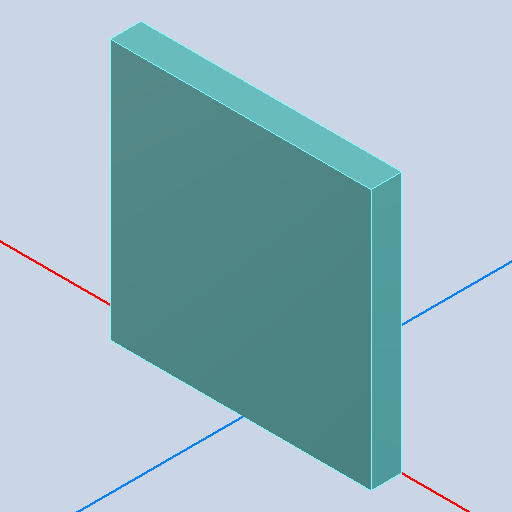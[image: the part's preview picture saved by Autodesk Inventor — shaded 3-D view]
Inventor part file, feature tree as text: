
AUTODESK INVENTOR PART (.ipt)
format: ipt  version: 2022 (Build 260153000, 153)  size: 92,672 bytes
history: native  units: mm
features: other x2, extrude x1
ambient origin geometry x8: Origin, YZ Plane, XZ Plane, XY Plane, X Axis, Y Axis, Z Axis, Center Point
bodies: Body1 (feature_tree)
feature tree (3):
  other  "Твердое тело1"
  extrude  "Выдавливание1"  Depth=1.0mm TaperAngle=0.0deg
  other  "153CLV-0810, 153CLV-0810_10"
